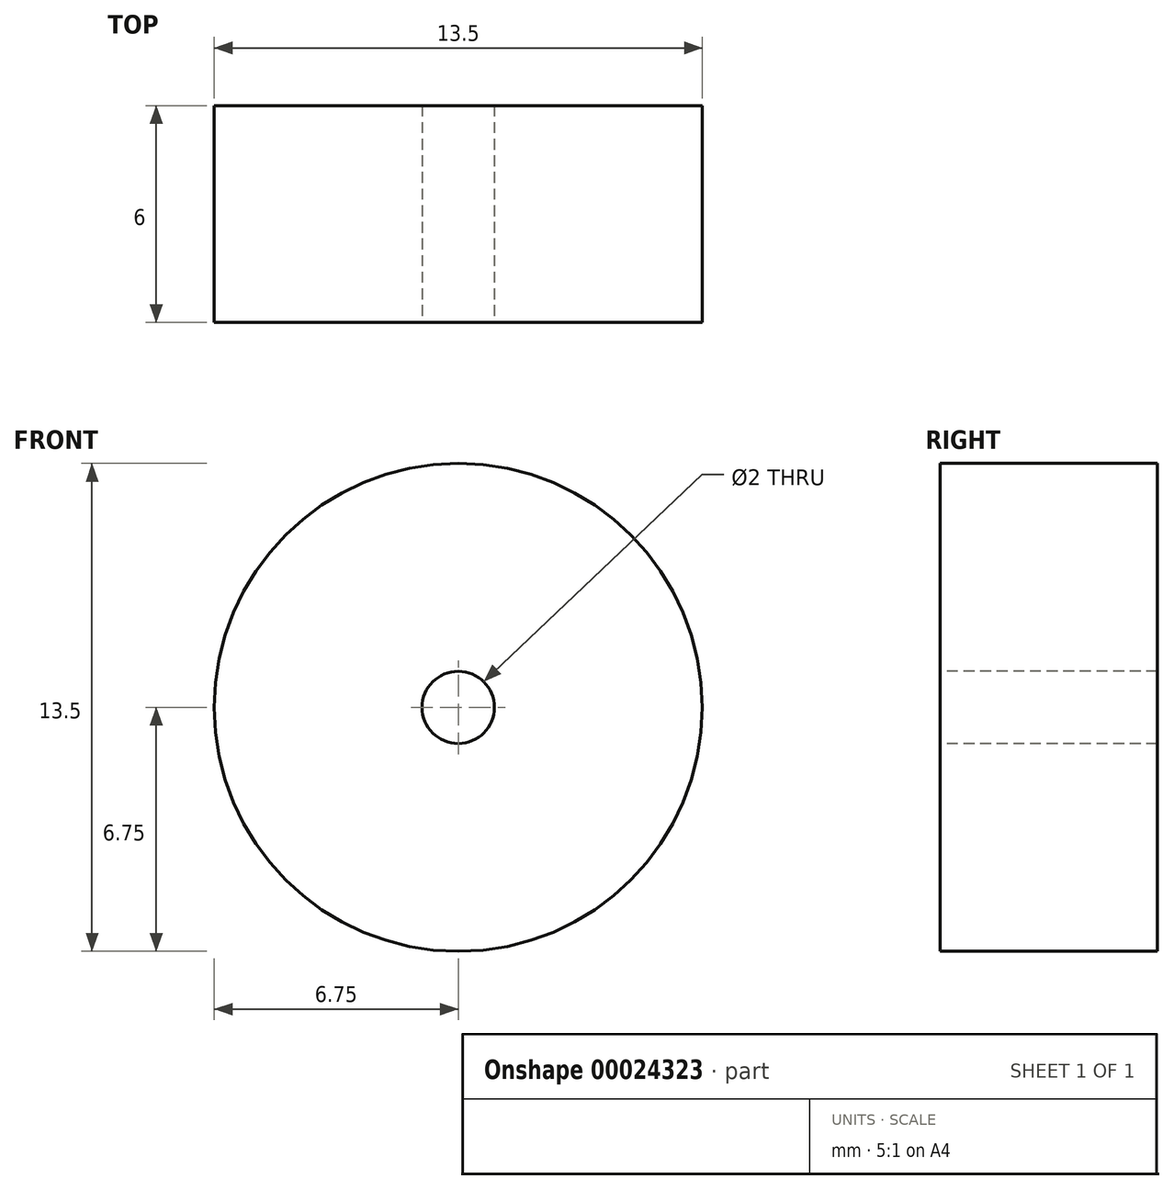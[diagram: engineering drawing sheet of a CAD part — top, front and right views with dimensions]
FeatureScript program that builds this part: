
annotation { "Feature Type Name" : "Feature", "Feature Type Description" : "" }
export const myFeature = defineFeature(function(context is Context, id is Id, definition is map)
    precondition{}
    {
        {
            var Q0;
            Q0=qCreatedBy(makeId("Right.planeOp"),FACE);
            var sketch = newSketch(context, id + "F0", { "sketchPlane" : qUnion([Q0])});
            skLineSegment(sketch, "E0", {"start": v(-12.28, 0) * mm, "end": v(12.28, 0) * mm, "construction": true});
            skLineSegment(sketch, "E1.bottom", {"start": v(-3.08, 1) * mm, "end": v(2.92, 1) * mm});
            skLineSegment(sketch, "E1.top", {"start": v(-3.08, 6.75) * mm, "end": v(2.92, 6.75) * mm});
            skLineSegment(sketch, "E1.left", {"start": v(-3.08, 1) * mm, "end": v(-3.08, 6.75) * mm});
            skLineSegment(sketch, "E1.right", {"start": v(2.92, 1) * mm, "end": v(2.92, 6.75) * mm});
            skSolve(sketch);
        }
        {
            var Q0;
            Q0 = qSketchRegion(id + "F0", true);
            var Q1;
            Q1=sQuery(id+"F0.wireOp",EDGE,"E0");
            revolve(context, id + "F1", {"entities" : qUnion([Q0]), "axis" : qUnion([Q1]), "revolveType" : RevolveType.FULL});
        }
    });
